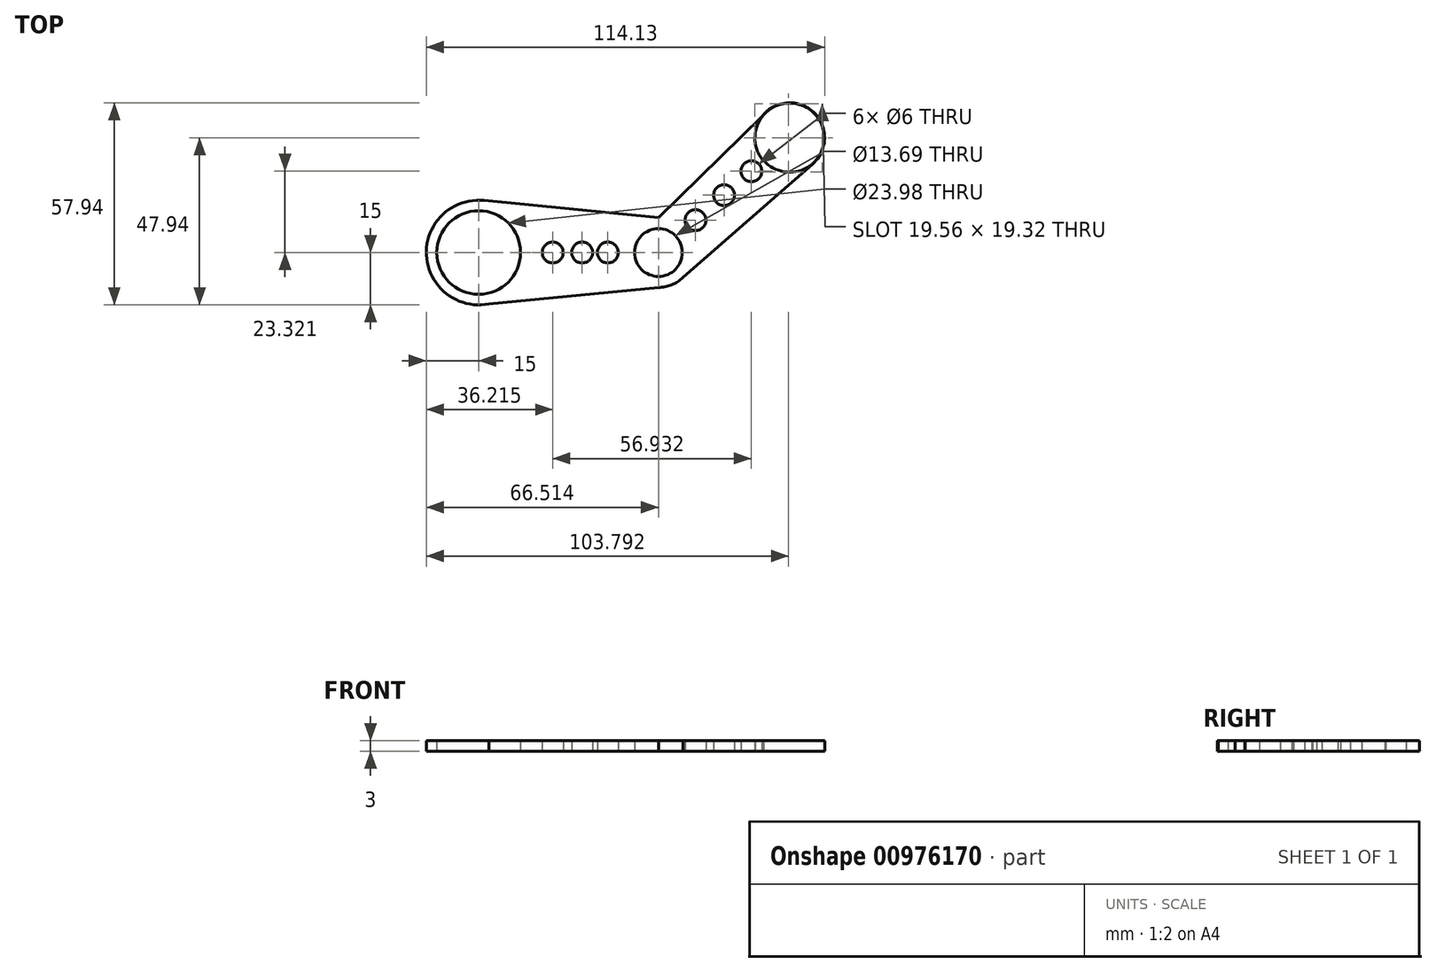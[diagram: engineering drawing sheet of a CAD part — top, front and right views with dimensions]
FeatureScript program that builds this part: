
annotation { "Feature Type Name" : "Feature", "Feature Type Description" : "" }
export const myFeature = defineFeature(function(context is Context, id is Id, definition is map)
    precondition{}
    {
        {
            var Q0;
            Q0=qCreatedBy(makeId("Top.planeOp"),FACE);
            var sketch = newSketch(context, id + "F0", { "sketchPlane" : qUnion([Q0])});
            skCircle(sketch, "E0", {"center": v(-15, 0) * mm, "radius": 15 * mm});
            skCircle(sketch, "E1", {"center": v(36.51, 0) * mm, "radius": 10 * mm});
            skPoint(sketch, "E2", {"position": v(36.51, 10) * mm});
            skPoint(sketch, "E3", {"position": v(-13.49, 14.92) * mm});
            skPoint(sketch, "E4", {"position": v(36.51, 14.92) * mm});
            skCircle(sketch, "E5", {"center": v(74.13, 32.94) * mm, "radius": 10 * mm});
            skPoint(sketch, "E6", {"position": v(74.13, 22.94) * mm});
            skPoint(sketch, "E7", {"position": v(-15, -15) * mm});
            skPoint(sketch, "E8", {"position": v(-30, 0) * mm});
            skPoint(sketch, "E9", {"position": v(26.51, 0) * mm});
            skPoint(sketch, "E10", {"position": v(36.51, -10) * mm});
            skPoint(sketch, "E11", {"position": v(46.51, 0) * mm});
            skPoint(sketch, "E12", {"position": v(64.13, 32.94) * mm});
            skPoint(sketch, "E13", {"position": v(84.13, 32.94) * mm});
            skPoint(sketch, "E14", {"position": v(74.13, 42.94) * mm});
            skLineSegment(sketch, "E15", {"start": v(-13.49, 14.92) * mm, "end": v(36.51, 10) * mm});
            skLineSegment(sketch, "E16", {"start": v(64.13, 32.94) * mm, "end": v(66.23, 39.07) * mm});
            skLineSegment(sketch, "E17", {"start": v(66.23, 39.07) * mm, "end": v(64.13, 32.94) * mm});
            skLineSegment(sketch, "E18", {"start": v(36.51, 10) * mm, "end": v(66.23, 39.07) * mm});
            skLineSegment(sketch, "E19", {"start": v(42.67, -7.88) * mm, "end": v(80.72, 25.41) * mm});
            skLineSegment(sketch, "E20", {"start": v(80.72, 25.41) * mm, "end": v(42.67, -7.88) * mm});
            skLineSegment(sketch, "E21", {"start": v(36.51, -10) * mm, "end": v(-15, -15) * mm});
            skCircle(sketch, "E22", {"center": v(6.22, 0) * mm, "radius": 3 * mm});
            skCircle(sketch, "E23", {"center": v(14.65, 0) * mm, "radius": 3 * mm});
            skCircle(sketch, "E24", {"center": v(22, 0) * mm, "radius": 3 * mm});
            skPoint(sketch, "E25", {"position": v(6.22, 3) * mm});
            skPoint(sketch, "E26", {"position": v(14.65, 3) * mm});
            skPoint(sketch, "E27", {"position": v(22, 3) * mm});
            skLineSegment(sketch, "E28", {"start": v(36.51, 0) * mm, "end": v(74.13, 32.94) * mm});
            skCircle(sketch, "E29", {"center": v(55.32, 16.47) * mm, "radius": 3 * mm});
            skCircle(sketch, "E30", {"center": v(63.15, 23.32) * mm, "radius": 3 * mm});
            skCircle(sketch, "E31", {"center": v(47.12, 9.3) * mm, "radius": 3 * mm});
            skPoint(sketch, "E32", {"position": v(50.12, 9.3) * mm});
            skPoint(sketch, "E33", {"position": v(58.32, 16.47) * mm});
            skPoint(sketch, "E34", {"position": v(66.15, 23.32) * mm});
            skCircle(sketch, "E35", {"center": v(-15, 0) * mm, "radius": 12 * mm});
            skCircle(sketch, "E36", {"center": v(36.51, 0) * mm, "radius": 6.84 * mm});
            skCircle(sketch, "E37", {"center": v(74.13, 32.94) * mm, "radius": 9.9 * mm});
            skCircle(sketch, "E38", {"center": v(74.13, 32.94) * mm, "radius": 6.77 * mm});
            skSolve(sketch);
        }
        {
            var Q0;
            Q0 = qSketchRegion(id + "F0", true);
            extrude(context, id + "F1", {"entities" : qUnion([Q0]), "depth" : 3 * mm, "offsetDistance" : 25 * mm});
        }
    });
